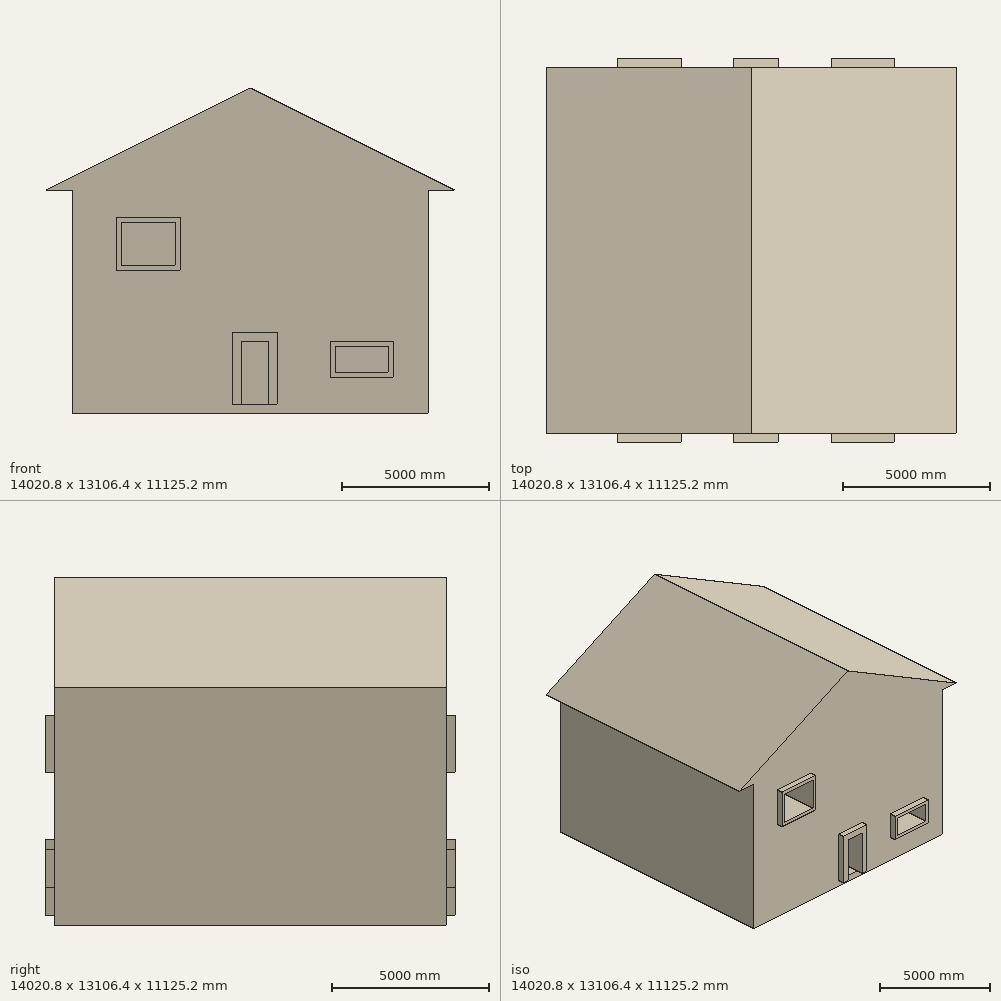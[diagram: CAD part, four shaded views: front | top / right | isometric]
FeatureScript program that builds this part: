
annotation { "Feature Type Name" : "Feature", "Feature Type Description" : "" }
export const myFeature = defineFeature(function(context is Context, id is Id, definition is map)
    precondition{}
    {
        {
            var Q0;
            Q0=qCreatedBy(makeId("Front.planeOp"),FACE);
            var sketch = newSketch(context, id + "F0", { "sketchPlane" : qUnion([Q0])});
            skLineSegment(sketch, "E0", {"start": v(0, 0) * mm, "end": v(-6096, 0) * mm});
            skLineSegment(sketch, "E1", {"start": v(0, 0) * mm, "end": v(6096, 0) * mm});
            skLineSegment(sketch, "E2", {"start": v(0, 0) * mm, "end": v(0, 3048) * mm, "construction": true});
            skLineSegment(sketch, "E3", {"start": v(0, 3048) * mm, "end": v(-6096, 0) * mm});
            skLineSegment(sketch, "E4", {"start": v(0, 3048) * mm, "end": v(6096, 0) * mm});
            skLineSegment(sketch, "E5", {"start": v(6096, 0) * mm, "end": v(7010.4, 0) * mm});
            skLineSegment(sketch, "E6", {"start": v(0, 3048) * mm, "end": v(0, 3505.2) * mm});
            skLineSegment(sketch, "E7", {"start": v(0, 3505.2) * mm, "end": v(7010.4, 0) * mm});
            skLineSegment(sketch, "E8", {"start": v(-6096, 0) * mm, "end": v(-6096, -7315.2) * mm});
            skLineSegment(sketch, "E9", {"start": v(-6096, -7315.2) * mm, "end": v(6096, -7315.2) * mm});
            skLineSegment(sketch, "E10", {"start": v(6096, 0) * mm, "end": v(6096, -7315.2) * mm});
            skLineSegment(sketch, "E11", {"start": v(-6096, -7315.2) * mm, "end": v(-6096, -7620) * mm});
            skLineSegment(sketch, "E12", {"start": v(-6096, -7620) * mm, "end": v(6096, -7620) * mm});
            skLineSegment(sketch, "E13", {"start": v(6096, -7620) * mm, "end": v(6096, -7315.2) * mm});
            skLineSegment(sketch, "E14", {"start": v(152.4, -5181.6) * mm, "end": v(-304.8, -5181.6) * mm});
            skLineSegment(sketch, "E15", {"start": v(-304.8, -5181.6) * mm, "end": v(-304.8, -7315.2) * mm});
            skLineSegment(sketch, "E16", {"start": v(152.4, -5181.6) * mm, "end": v(609.6, -5181.6) * mm});
            skLineSegment(sketch, "E17", {"start": v(609.6, -5181.6) * mm, "end": v(609.6, -7315.2) * mm});
            skLineSegment(sketch, "E18", {"start": v(-6096, 0) * mm, "end": v(-7010.4, 0) * mm});
            skLineSegment(sketch, "E19", {"start": v(-7010.4, 0) * mm, "end": v(0, 3505.2) * mm});
            skLineSegment(sketch, "E20.bottom", {"start": v(2743.2, -5181.6) * mm, "end": v(4876.8, -5181.6) * mm});
            skLineSegment(sketch, "E20.top", {"start": v(2743.2, -6400.8) * mm, "end": v(4876.8, -6400.8) * mm});
            skLineSegment(sketch, "E20.left", {"start": v(2743.2, -5181.6) * mm, "end": v(2743.2, -6400.8) * mm});
            skLineSegment(sketch, "E20.right", {"start": v(4876.8, -5181.6) * mm, "end": v(4876.8, -6400.8) * mm});
            skLineSegment(sketch, "E21.0", {"start": v(2912.36, -5350.76) * mm, "end": v(4707.64, -5350.76) * mm});
            skLineSegment(sketch, "E21.1", {"start": v(2912.36, -5350.76) * mm, "end": v(2912.36, -6231.64) * mm});
            skLineSegment(sketch, "E21.2", {"start": v(2912.36, -6231.64) * mm, "end": v(4707.64, -6231.64) * mm});
            skLineSegment(sketch, "E21.3", {"start": v(4707.64, -5350.76) * mm, "end": v(4707.64, -6231.64) * mm});
            skLineSegment(sketch, "E22.0", {"start": v(914.4, -4876.8) * mm, "end": v(914.4, -7315.2) * mm});
            skLineSegment(sketch, "E22.1", {"start": v(152.4, -4876.8) * mm, "end": v(914.4, -4876.8) * mm});
            skLineSegment(sketch, "E22.2", {"start": v(152.4, -4876.8) * mm, "end": v(-609.6, -4876.8) * mm});
            skLineSegment(sketch, "E22.3", {"start": v(-609.6, -4876.8) * mm, "end": v(-609.6, -7315.2) * mm});
            skLineSegment(sketch, "E23.bottom", {"start": v(-4572, -914.4) * mm, "end": v(-2404.87, -914.4) * mm});
            skLineSegment(sketch, "E23.top", {"start": v(-4572, -2743.2) * mm, "end": v(-2404.87, -2743.2) * mm});
            skLineSegment(sketch, "E23.left", {"start": v(-4572, -914.4) * mm, "end": v(-4572, -2743.2) * mm});
            skLineSegment(sketch, "E23.right", {"start": v(-2404.87, -914.4) * mm, "end": v(-2404.87, -2743.2) * mm});
            skLineSegment(sketch, "E24.0", {"start": v(-2574.04, -1083.56) * mm, "end": v(-2574.04, -2574.04) * mm});
            skLineSegment(sketch, "E24.1", {"start": v(-4402.84, -1083.56) * mm, "end": v(-2574.04, -1083.56) * mm});
            skLineSegment(sketch, "E24.2", {"start": v(-4402.84, -1083.56) * mm, "end": v(-4402.84, -2574.04) * mm});
            skLineSegment(sketch, "E24.3", {"start": v(-4402.84, -2574.04) * mm, "end": v(-2574.04, -2574.04) * mm});
            skSolve(sketch);
        }
        {
            var Q0;
            Q0=makeQuery(id+"F0.imprint","IMPRINT",FACE,{"disambiguationData":[TD([[makeQuery(id+"F0.imprint","IMPRINT",EDGE,{"derivedFrom":sQuery(id+"F0.wireOp",EDGE,"E3")}),-1.0]])]});
            var Q1;
            Q1=makeQuery(id+"F0.imprint","IMPRINT",FACE,{"disambiguationData":[TD([[makeQuery(id+"F0.imprint","IMPRINT",EDGE,{"derivedFrom":sQuery(id+"F0.wireOp",EDGE,"E4")}),1.0]])]});
            extrude(context, id + "F1", {"entities" : qUnion([Q0, Q1]), "endBound" : BoundingType.SYMMETRIC, "depth" : 12496.8 * mm, "offsetDistance" : 30.48 * mm});
        }
        {
            var Q0;
            Q0=makeQuery(id+"F0.imprint","IMPRINT",FACE,{"disambiguationData":[TD([[makeQuery(id+"F0.imprint","IMPRINT",EDGE,{"derivedFrom":sQuery(id+"F0.wireOp",EDGE,"E0")}),-1.0]])]});
            extrude(context, id + "F2", {"entities" : qUnion([Q0]), "operationType" : NewBodyOperationType.ADD, "endBound" : BoundingType.SYMMETRIC, "depth" : 12496.8 * mm, "offsetDistance" : 30.48 * mm});
        }
        {
            var Q0;
            Q0=makeQuery(id+"F0.imprint","IMPRINT",FACE,{"disambiguationData":[TD([[makeQuery(id+"F0.imprint","IMPRINT",EDGE,{"derivedFrom":sQuery(id+"F0.wireOp",EDGE,"E0")}),1.0]])]});
            extrude(context, id + "F3", {"entities" : qUnion([Q0]), "operationType" : NewBodyOperationType.ADD, "endBound" : BoundingType.SYMMETRIC, "depth" : 12496.8 * mm, "offsetDistance" : 30.48 * mm});
        }
        {
            var Q0;
            {var subQ5=sQuery(id+"F0.wireOp",EDGE,"E11");Q0=makeQuery(id+"F0.imprint","IMPRINT",FACE,{"disambiguationData":[TD([[makeQuery(id+"F0.imprint","IMPRINT",EDGE,{"derivedFrom":subQ5}),1.0]])]});}
            extrude(context, id + "F4", {"entities" : qUnion([Q0]), "operationType" : NewBodyOperationType.ADD, "endBound" : BoundingType.SYMMETRIC, "depth" : 12496.8 * mm, "offsetDistance" : 30.48 * mm});
        }
        {
            var Q0;
            Q0=makeQuery(id+"F0.imprint","IMPRINT",FACE,{"disambiguationData":[TD([[makeQuery(id+"F0.imprint","IMPRINT",EDGE,{"derivedFrom":sQuery(id+"F0.wireOp",EDGE,"E24.0")}),-1.0]])]});
            var Q1;
            Q1=makeQuery(id+"F0.imprint","IMPRINT",FACE,{"disambiguationData":[TD([[makeQuery(id+"F0.imprint","IMPRINT",EDGE,{"derivedFrom":sQuery(id+"F0.wireOp",EDGE,"E21.0")}),-1.0]])]});
            var Q2;
            Q2=makeQuery(id+"F0.imprint","IMPRINT",FACE,{"disambiguationData":[TD([[makeQuery(id+"F0.imprint","IMPRINT",EDGE,{"derivedFrom":sQuery(id+"F0.wireOp",EDGE,"E14")}),1.0]])]});
            extrude(context, id + "F5", {"entities" : qUnion([Q0, Q1, Q2]), "operationType" : NewBodyOperationType.ADD, "endBound" : BoundingType.SYMMETRIC, "depth" : 1036.32 * mm, "offsetDistance" : 30.48 * mm});
        }
        {
            var Q0;
            Q0=makeQuery(id+"F0.imprint","IMPRINT",FACE,{"disambiguationData":[TD([[makeQuery(id+"F0.imprint","IMPRINT",EDGE,{"derivedFrom":sQuery(id+"F0.wireOp",EDGE,"E23.bottom")}),-1.0]])]});
            var Q1;
            Q1=makeQuery(id+"F0.imprint","IMPRINT",FACE,{"disambiguationData":[TD([[makeQuery(id+"F0.imprint","IMPRINT",EDGE,{"derivedFrom":sQuery(id+"F0.wireOp",EDGE,"E14")}),-1.0]])]});
            var Q2;
            Q2=makeQuery(id+"F0.imprint","IMPRINT",FACE,{"disambiguationData":[TD([[makeQuery(id+"F0.imprint","IMPRINT",EDGE,{"derivedFrom":sQuery(id+"F0.wireOp",EDGE,"E20.bottom")}),-1.0]])]});
            extrude(context, id + "F6", {"entities" : qUnion([Q0, Q1, Q2]), "endBound" : BoundingType.SYMMETRIC, "depth" : 13106.4 * mm, "offsetDistance" : 30.48 * mm});
        }
    });
